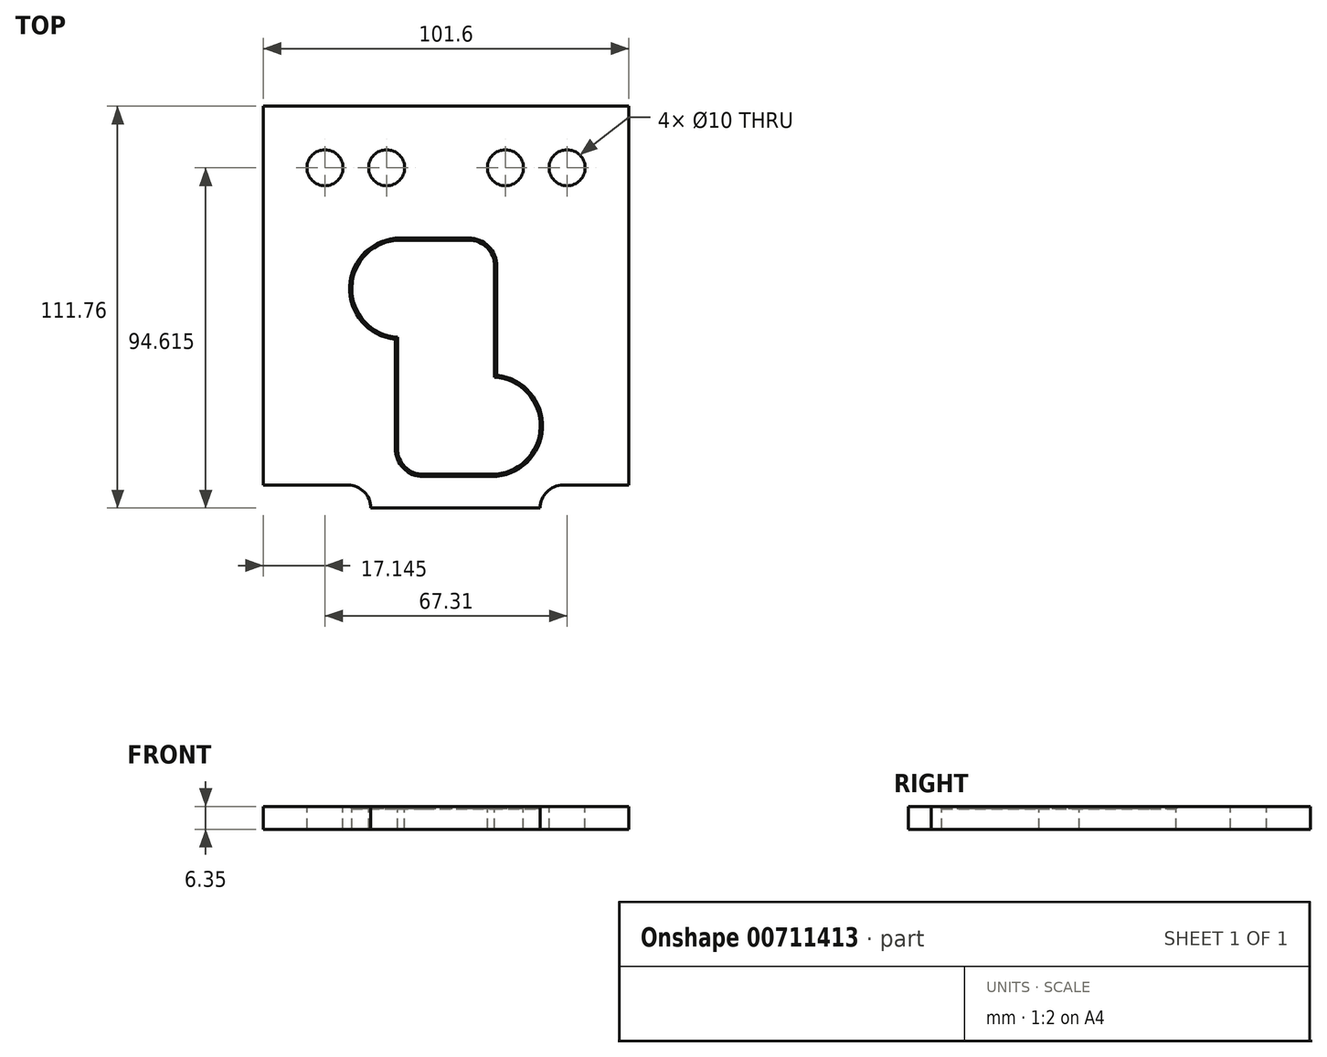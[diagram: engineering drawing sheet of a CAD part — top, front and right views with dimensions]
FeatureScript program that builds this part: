
annotation { "Feature Type Name" : "Feature", "Feature Type Description" : "" }
export const myFeature = defineFeature(function(context is Context, id is Id, definition is map)
    precondition{}
    {
        {
            var Q0;
            Q0=qCreatedBy(makeId("Top.planeOp"),FACE);
            var sketch = newSketch(context, id + "F0", { "sketchPlane" : qUnion([Q0])});
            skLineSegment(sketch, "E0.bottom", {"start": v(12.7, -31.75) * mm, "end": v(-6.35, -31.75) * mm});
            skLineSegment(sketch, "E0.top", {"start": v(6.35, 31.75) * mm, "end": v(-12.7, 31.75) * mm});
            skLineSegment(sketch, "E0.right", {"start": v(-12.7, -25.4) * mm, "end": v(-12.7, 6.35) * mm});
            skPoint(sketch, "E0.middle", {"position": v(0, 0) * mm});
            skArc(sketch, "E1", {"start": v(-12.7, 31.75) * mm, "mid": v(-25.4, 19.05) * mm, "end": v(-12.7, 6.35) * mm});
            skArc(sketch, "E2", {"start": v(12.7, -31.75) * mm, "mid": v(25.4, -19.05) * mm, "end": v(12.7, -6.35) * mm});
            skLineSegment(sketch, "E3.trimOffspring", {"start": v(12.7, -6.35) * mm, "end": v(12.7, 25.4) * mm});
            skPoint(sketch, "E4.visualSharp", {"position": v(-12.7, -31.75) * mm});
            skArc(sketch, "E4.filletArc", {"start": v(-12.7, -25.4) * mm, "mid": v(-10.84, -29.9) * mm, "end": v(-6.35, -31.75) * mm});
            skPoint(sketch, "E5.visualSharp", {"position": v(12.7, 31.75) * mm});
            skArc(sketch, "E5.filletArc", {"start": v(12.7, 25.4) * mm, "mid": v(10.84, 29.9) * mm, "end": v(6.35, 31.75) * mm});
            skLineSegment(sketch, "E6.bottom", {"start": v(0, -19.05) * mm, "end": v(-6.35, -19.05) * mm});
            skLineSegment(sketch, "E6.top", {"start": v(0, 19.05) * mm, "end": v(-6.35, 19.05) * mm});
            skLineSegment(sketch, "E6.left", {"start": v(6.35, -12.7) * mm, "end": v(6.35, 12.7) * mm});
            skLineSegment(sketch, "E6.right", {"start": v(-6.35, -19.05) * mm, "end": v(-6.35, 19.05) * mm});
            skPoint(sketch, "E7.visualSharp", {"position": v(6.35, 19.05) * mm});
            skArc(sketch, "E7.filletArc", {"start": v(6.35, 12.7) * mm, "mid": v(4.5, 17.2) * mm, "end": v(0, 19.05) * mm});
            skPoint(sketch, "E8.visualSharp", {"position": v(6.35, -19.05) * mm});
            skArc(sketch, "E8.filletArc", {"start": v(0, -19.05) * mm, "mid": v(4.5, -17.2) * mm, "end": v(6.35, -12.7) * mm});
            skArc(sketch, "E9.0", {"start": v(12.7, -32.54) * mm, "mid": v(26.19, -19.45) * mm, "end": v(13.5, -5.58) * mm});
            skLineSegment(sketch, "E9.1", {"start": v(12.7, -32.54) * mm, "end": v(-6.35, -32.54) * mm});
            skLineSegment(sketch, "E9.2", {"start": v(13.5, -5.58) * mm, "end": v(13.5, 25.4) * mm});
            skArc(sketch, "E9.3", {"start": v(-13.5, -25.4) * mm, "mid": v(-11.4, -30.45) * mm, "end": v(-6.35, -32.54) * mm});
            skArc(sketch, "E9.4", {"start": v(13.5, 25.4) * mm, "mid": v(11.4, 30.45) * mm, "end": v(6.35, 32.54) * mm});
            skLineSegment(sketch, "E9.5", {"start": v(6.35, 32.54) * mm, "end": v(-12.7, 32.54) * mm});
            skArc(sketch, "E9.6", {"start": v(-12.7, 32.54) * mm, "mid": v(-26.19, 19.45) * mm, "end": v(-13.5, 5.58) * mm});
            skLineSegment(sketch, "E9.7", {"start": v(-13.5, -25.4) * mm, "end": v(-13.5, 5.58) * mm});
            skLineSegment(sketch, "E10.top", {"start": v(-50.8, 69.85) * mm, "end": v(50.8, 69.85) * mm});
            skLineSegment(sketch, "E11", {"start": v(50.8, 69.85) * mm, "end": v(50.8, -35.56) * mm});
            skLineSegment(sketch, "E12", {"start": v(-50.8, 69.85) * mm, "end": v(-50.8, -35.56) * mm});
            skLineSegment(sketch, "E13", {"start": v(-50.8, 52.7) * mm, "end": v(50.8, 52.7) * mm});
            skLineSegment(sketch, "E14", {"start": v(-33.66, 69.85) * mm, "end": v(-33.66, 52.7) * mm});
            skLineSegment(sketch, "E15", {"start": v(-16.51, 69.85) * mm, "end": v(-16.51, 52.7) * mm});
            skLineSegment(sketch, "E16", {"start": v(16.5, 69.85) * mm, "end": v(16.5, 52.7) * mm});
            skLineSegment(sketch, "E17", {"start": v(33.65, 69.85) * mm, "end": v(33.65, 52.7) * mm});
            skCircle(sketch, "E18", {"center": v(-33.66, 52.7) * mm, "radius": 5 * mm});
            skCircle(sketch, "E19", {"center": v(-16.51, 52.7) * mm, "radius": 5 * mm});
            skCircle(sketch, "E20", {"center": v(16.5, 52.7) * mm, "radius": 5 * mm});
            skCircle(sketch, "E21", {"center": v(33.65, 52.7) * mm, "radius": 5 * mm});
            skLineSegment(sketch, "E22", {"start": v(-47.1, 37.46) * mm, "end": v(41.96, 37.46) * mm, "construction": true});
            skLineSegment(sketch, "E23", {"start": v(-50.8, -35.56) * mm, "end": v(-27.25, -35.56) * mm});
            skLineSegment(sketch, "E24", {"start": v(26.19, -18.65) * mm, "end": v(26.19, -35.56) * mm, "construction": true});
            skPoint(sketch, "E24.startSnap0", {"position": v(26.19, -19.45) * mm});
            skPoint(sketch, "E25.startSnap0", {"position": v(-25.4, 19.05) * mm});
            skLineSegment(sketch, "E26", {"start": v(-20.9, 8.33) * mm, "end": v(-20.9, -35.56) * mm, "construction": true});
            skLineSegment(sketch, "E27.top", {"start": v(-20.9, -41.91) * mm, "end": v(26.19, -41.91) * mm});
            skLineSegment(sketch, "E27.left", {"start": v(-20.9, -41.91) * mm, "end": v(-20.9, -41.91) * mm});
            skLineSegment(sketch, "E27.right", {"start": v(26.19, -41.91) * mm, "end": v(26.19, -41.91) * mm});
            skLineSegment(sketch, "E28.trimOffspring", {"start": v(32.54, -35.56) * mm, "end": v(50.8, -35.56) * mm});
            skPoint(sketch, "E29.visualSharp", {"position": v(26.19, -35.56) * mm});
            skArc(sketch, "E29.filletArc", {"start": v(32.54, -35.56) * mm, "mid": v(28.05, -37.42) * mm, "end": v(26.19, -41.91) * mm});
            skPoint(sketch, "E30.visualSharp", {"position": v(-20.9, -35.56) * mm});
            skArc(sketch, "E30.filletArc", {"start": v(-20.9, -41.91) * mm, "mid": v(-22.76, -37.42) * mm, "end": v(-27.25, -35.56) * mm});
            skSolve(sketch);
        }
        {
            var Q0;
            Q0 = qSketchRegion(id + "F0", true);
            extrude(context, id + "F1", {"entities" : qUnion([Q0]), "depth" : -6.35 * mm, "offsetDistance" : 25.4 * mm});
        }
        {
            var Q0;
            Q0=makeQuery(id+"F1.opExtrude","CAP_EDGE",EDGE,{"disambiguationData":[OSD([sQuery(id+"F0.wireOp",EDGE,"E9.2")])],"isStart":true});
            var Q1;
            Q1=makeQuery(id+"F1.opExtrude","CAP_EDGE",EDGE,{"disambiguationData":[OSD([sQuery(id+"F0.wireOp",EDGE,"E9.7")])],"isStart":true});
            chamfer(context, id + "F2", {"entities" : qUnion([Q0, Q1]), "width" : 0.64 * mm, "tangentPropagation" : true});
        }
    });
